# Revit family: Friction_towel_Hook-Bradley_Corp-Security-SA30
name_source: partatom
category: Specialty Equipment
revit_build: Autodesk Revit MEP 2012 (Build: 20110309_2315(x64)
units: mm (PartAtom-declared; Revit-internal decimal feet)

## types (1)
- SA30
    ADA Compliant = No
    Assembly Code = C1030200
    Backplate Material = Metal - Bradley Corp - Stainless Steel - Satin
    Buy American Act = Yes
    Default Elevation = 48 "
    Depth = 1.313 "
    Description = Security Towel Hook
    Height = 5 "
    Hook Material = Metal - Bradley Corp - Brass - Chrome Plated
    Low Emitting Finish = No
    Low Emitting Material = No
    Manufacturer = Bradley Corporation
    MasterFormat Number = 10 28 13.53
    MasterFormat Title = Security Toilet Accessories
    Model = SA30
    OmniClass Table 21 Number = 21-03 10 90 40
    OmniClass Table 21 Title = Toilet, Bath, and Laundry Accessories
    OmniClass Table 23 Number = 23.31.25.27
    OmniClass Table 23 Title = Robe Hooks
    Percentage of Recycled Content = 0
    Product Tech Data URL - English = http://bradleycorp.com
    Specifications URL = http://www.bradleycorp.com
    URL = http://www.bradleycorp.com
    Version = 2.0
    Warranty Information = Complete Unit - One Year
    Width = 5 "

## geometry (parser evidence)
native form markers: Blend x8, Sweep x1
no freeform markers — native parametric forms only
